# Revit family: Überwurfmuffe
name_source: partatom
category: HLS-Bauteile
revit_build: Autodesk Revit 2017 (Build: 20190507_1515(x64)
units: mm (PartAtom-declared; Revit-internal decimal feet)

## family parameters
Arbeitsebenenbasiert = Nein
Beim Laden mit Abzugskörper schneiden = Nein
Bemaßung runder Anschluss = Durchmesser verwenden
Gemeinsam genutzt = Ja
Immer vertikal = Nein
Raumberechnungspunkt = Nein
Teiletyp = Normal

## types (2) — shared parameters
D = 26 mm
D0 = 23 mm
Fabrikat = MEFA
Firma = MEFA Befestigungs- und Montagesysteme GmbH
Gewicht = 0.08 kg
Gewicht pro Bauteil = 0.08 kg
Innengewinde 2 = 1/2''
Kurztext1 = Überwurfmuffe rund
L1 = 20 mm  [stored 0.0656168 ft]
L2 = 16 mm  [stored 0.0524934 ft]
Länge = 36 mm  [stored 0.11811 ft]
Länge Innengewinde 1 = 6 mm
Länge Innengewinde 2 = 15 mm
Material = Stahl
Mengeneinheit = St
Oberflaeche = galvanisch verzinkt
vpe = 50 St

## per-type parameters (varying)
| type | Artikelnummer | EAN | Innengewinde 1 | Kurztext2 | d1 |
| Überwurfmuffe M 8/ 1/2" | 0590304 | 4250928415134 | M8 | Innengew. M8 Innengew. 1/2'' L=36 mm | 7 mm  [stored 0.0229659 ft] |
| Überwurfmuffe M10/ 1/2" | 0590401 | 4250928415141 | M10 | Innengew. M10 Innengew. 1/2'' L=36 mm | 8 mm  [stored 0.0262467 ft] |

note: [stored X ft] marks values corroborated as IEEE doubles in the binary element streams (Revit-internal decimal feet)
